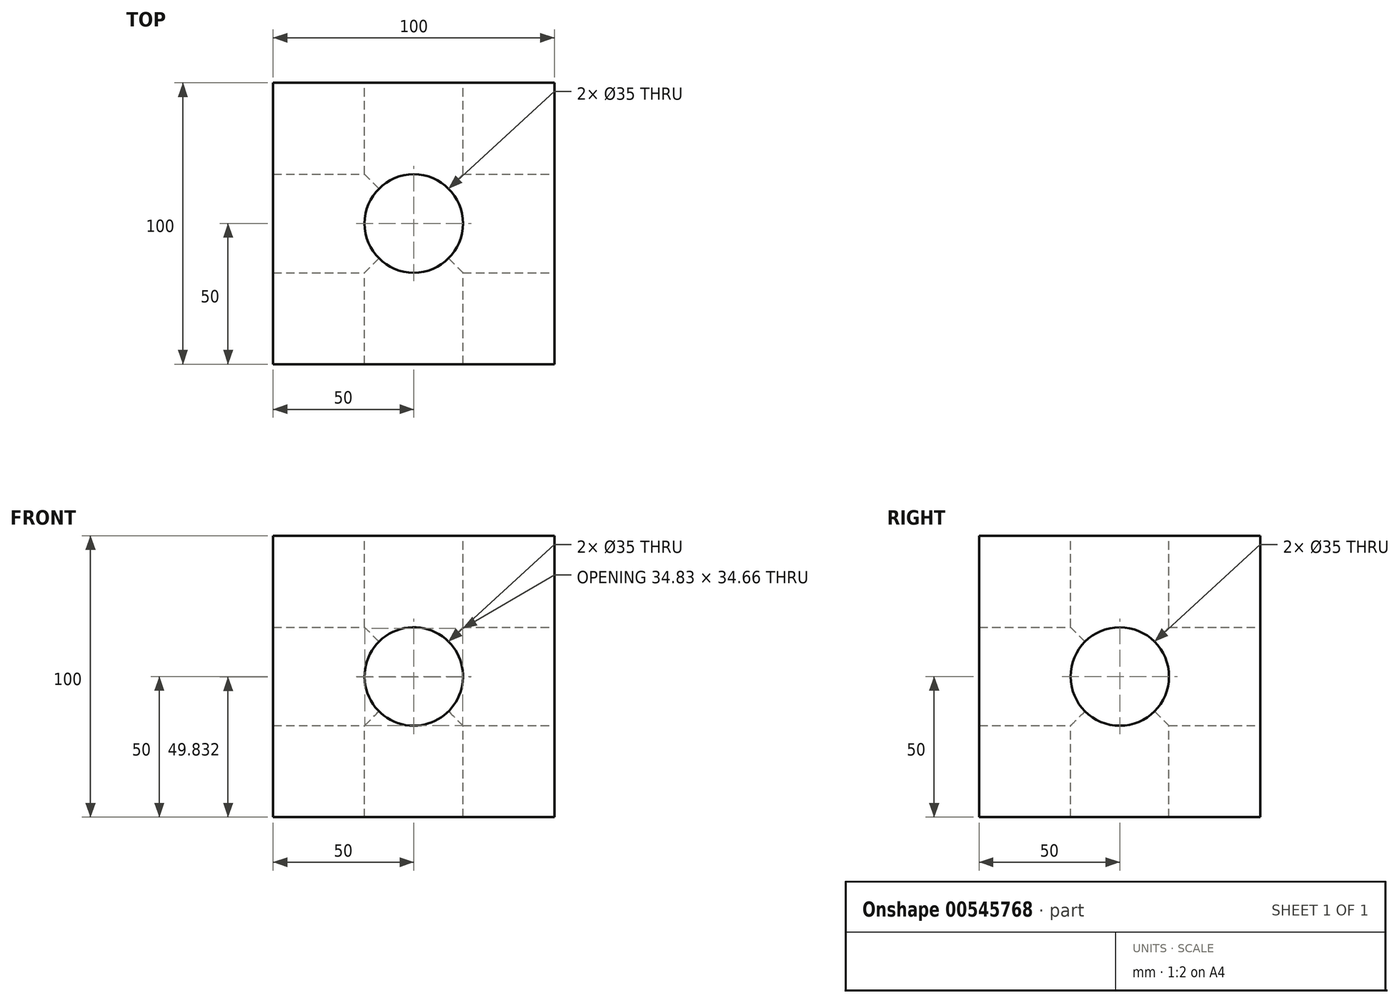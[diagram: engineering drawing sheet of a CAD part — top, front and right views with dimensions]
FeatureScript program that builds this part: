
annotation { "Feature Type Name" : "Feature", "Feature Type Description" : "" }
export const myFeature = defineFeature(function(context is Context, id is Id, definition is map)
    precondition{}
    {
        {
            var Q0;
            Q0=qCreatedBy(makeId("Front.planeOp"),FACE);
            var sketch = newSketch(context, id + "F0", { "sketchPlane" : qUnion([Q0])});
            skLineSegment(sketch, "E0.bottom", {"start": v(-50, 50) * mm, "end": v(50, 50) * mm});
            skLineSegment(sketch, "E0.top", {"start": v(-50, -50) * mm, "end": v(50, -50) * mm});
            skLineSegment(sketch, "E0.left", {"start": v(-50, 50) * mm, "end": v(-50, -50) * mm});
            skLineSegment(sketch, "E0.right", {"start": v(50, 50) * mm, "end": v(50, -50) * mm});
            skPoint(sketch, "E0.middle", {"position": v(0, 0) * mm});
            skCircle(sketch, "E1", {"center": v(0, 0) * mm, "radius": 17.5 * mm});
            skSolve(sketch);
        }
        {
            var Q0;
            Q0 = qSketchRegion(id + "F0", true);
            extrude(context, id + "F1", {"entities" : qUnion([Q0]), "endBound" : BoundingType.SYMMETRIC, "depth" : 100 * mm, "offsetDistance" : 25 * mm});
        }
        {
            var Q0;
            Q0=makeQuery(id+"F1.opExtrude","SWEPT_FACE",FACE,{"disambiguationData":[OSD([sQuery(id+"F0.wireOp",EDGE,"E0.right")])]});
            var sketch = newSketch(context, id + "F2", { "sketchPlane" : qUnion([Q0])});
            skCircle(sketch, "E2", {"center": v(0, 0) * mm, "radius": 17.5 * mm});
            skSolve(sketch);
        }
        {
            var Q0;
            Q0=makeQuery(id+"F2.imprint","IMPRINT",FACE,{"disambiguationData":[TD([[makeQuery(id+"F2.imprint","IMPRINT",EDGE,{"derivedFrom":sQuery(id+"F2.wireOp",EDGE,"E2")}),1.0]])]});
            var Q1;
            Q1=makeQuery(id+"F1.opExtrude","SWEPT_FACE",FACE,{"disambiguationData":[OSD([sQuery(id+"F0.wireOp",EDGE,"E0.left")])]});
            extrude(context, id + "F3", {"entities" : qUnion([Q0]), "operationType" : NewBodyOperationType.REMOVE, "endBound" : BoundingType.UP_TO_SURFACE, "oppositeDirection" : true, "depth" : 25 * mm, "endBoundEntityFace" : qUnion([Q1]), "offsetDistance" : 25 * mm});
        }
        {
            var Q0;
            Q0=makeQuery(id+"F1.opExtrude","SWEPT_FACE",FACE,{"disambiguationData":[OSD([sQuery(id+"F0.wireOp",EDGE,"E0.bottom")])]});
            var sketch = newSketch(context, id + "F4", { "sketchPlane" : qUnion([Q0])});
            skCircle(sketch, "E3", {"center": v(0, 0) * mm, "radius": 17.5 * mm});
            skSolve(sketch);
        }
        {
            var Q0;
            Q0=makeQuery(id+"F4.imprint","IMPRINT",FACE,{"disambiguationData":[TD([[makeQuery(id+"F4.imprint","IMPRINT",EDGE,{"derivedFrom":sQuery(id+"F4.wireOp",EDGE,"E3")}),1.0]])]});
            var Q1;
            Q1=makeQuery(id+"F1.opExtrude","SWEPT_FACE",FACE,{"disambiguationData":[OSD([sQuery(id+"F0.wireOp",EDGE,"E0.top")])]});
            extrude(context, id + "F5", {"entities" : qUnion([Q0]), "operationType" : NewBodyOperationType.REMOVE, "endBound" : BoundingType.UP_TO_SURFACE, "oppositeDirection" : true, "depth" : 25 * mm, "endBoundEntityFace" : qUnion([Q1]), "offsetDistance" : 25 * mm});
        }
    });
